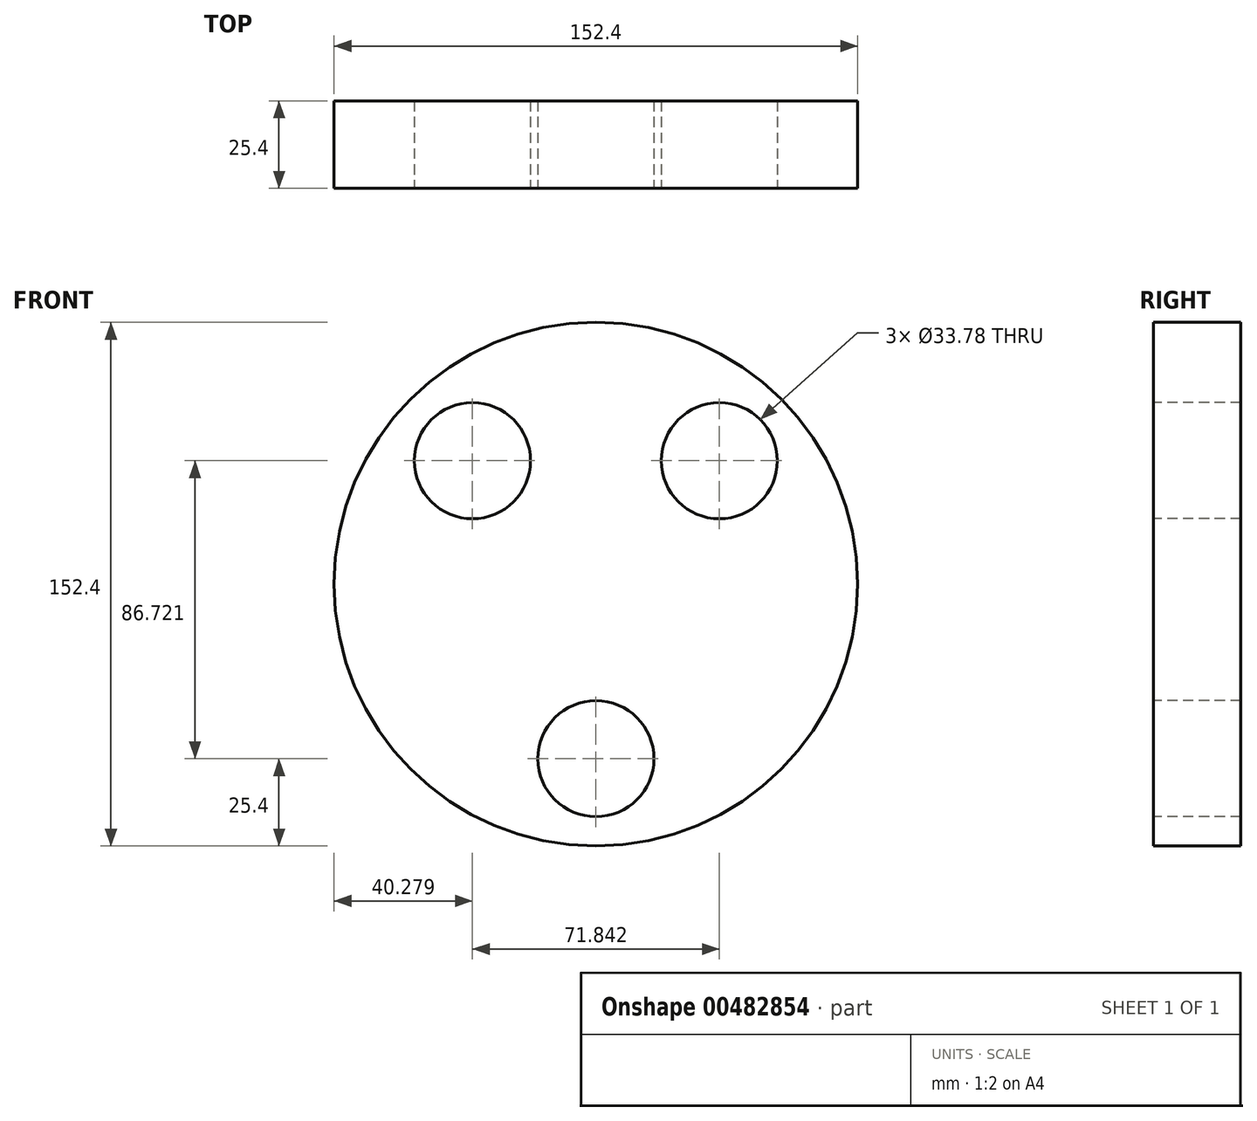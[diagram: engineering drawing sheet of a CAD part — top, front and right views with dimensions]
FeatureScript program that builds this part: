
annotation { "Feature Type Name" : "Feature", "Feature Type Description" : "" }
export const myFeature = defineFeature(function(context is Context, id is Id, definition is map)
    precondition{}
    {
        {
            var Q0;
            Q0=qCreatedBy(makeId("Front.planeOp"),FACE);
            var sketch = newSketch(context, id + "F0", { "sketchPlane" : qUnion([Q0])});
            skCircle(sketch, "E0", {"center": v(0, 0) * mm, "radius": 76.2 * mm});
            skSolve(sketch);
        }
        {
            var Q0;
            Q0 = qSketchRegion(id + "F0", true);
            extrude(context, id + "F1", {"entities" : qUnion([Q0]), "depth" : 25.4 * mm});
        }
        {
            var Q0;
            Q0=makeQuery(id+"F1.opExtrude","CAP_FACE",FACE,{"disambiguationData":[OSD([sQuery(id+"F0.wireOp",EDGE,"E0")])],"isStart":false});
            var sketch = newSketch(context, id + "F2", { "sketchPlane" : qUnion([Q0])});
            skCircle(sketch, "E1.1.0", {"center": v(-35.92, 35.92) * mm, "radius": 16.9 * mm});
            skCircle(sketch, "E1.4.0", {"center": v(0, -50.8) * mm, "radius": 16.9 * mm});
            skCircle(sketch, "E1.7.0", {"center": v(35.92, 35.92) * mm, "radius": 16.9 * mm});
            skPoint(sketch, "E1.center", {"position": v(0, 0) * mm});
            skPoint(sketch, "E2.center.orphan", {"position": v(0, 50.8) * mm});
            skSolve(sketch);
        }
        {
            var Q0;
            Q0 = qSketchRegion(id + "F2", true);
            extrude(context, id + "F3", {"entities" : qUnion([Q0]), "operationType" : NewBodyOperationType.REMOVE, "oppositeDirection" : true, "depth" : 25.4 * mm});
        }
    });
